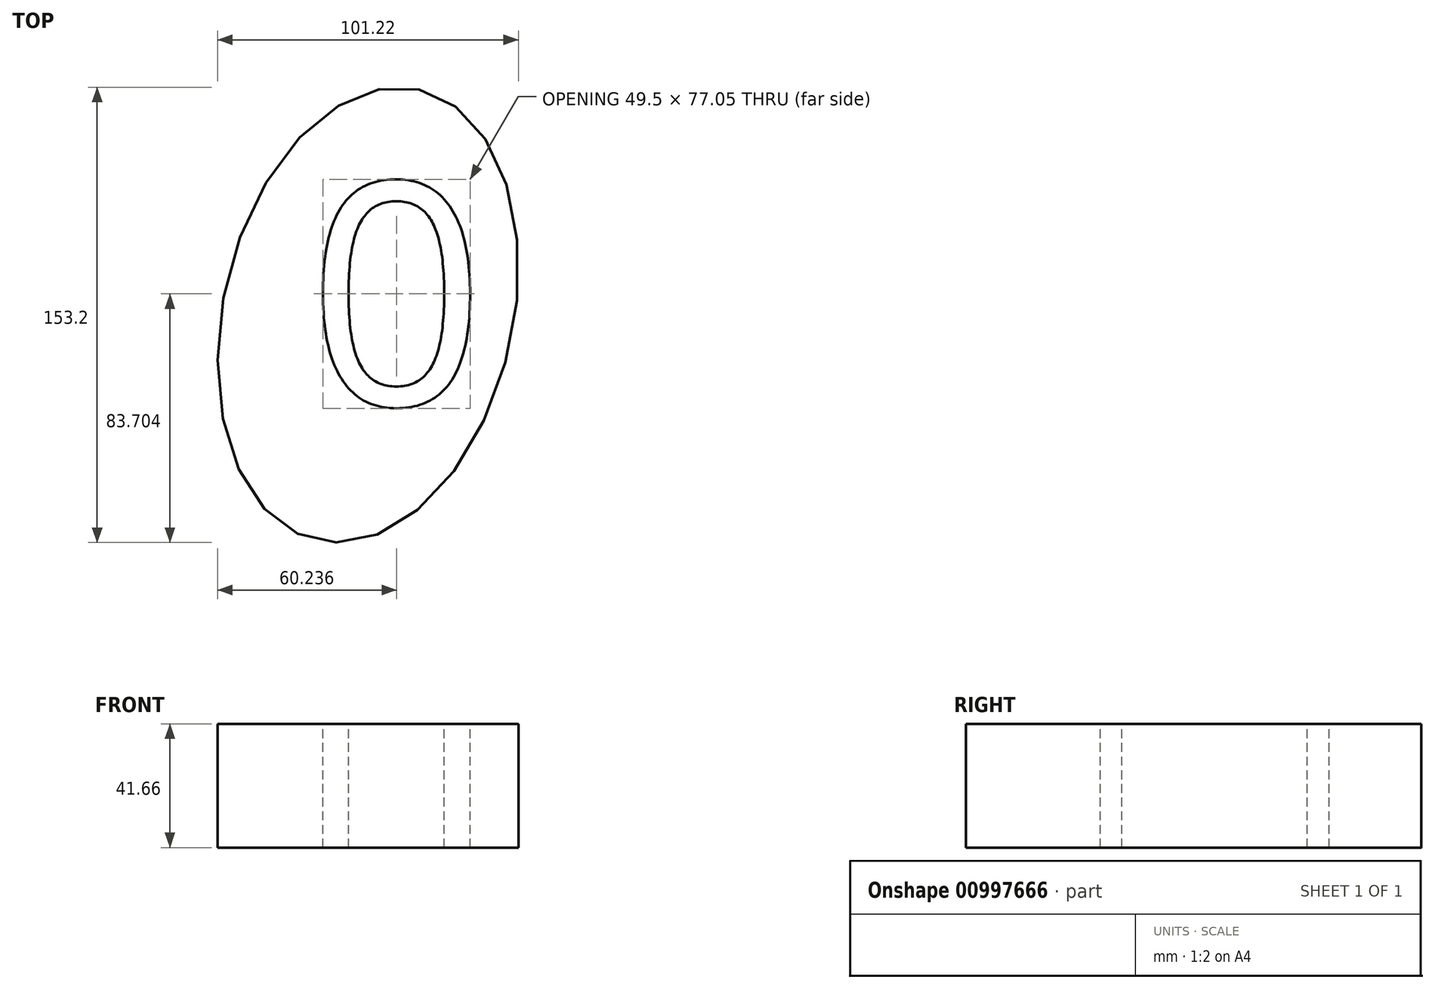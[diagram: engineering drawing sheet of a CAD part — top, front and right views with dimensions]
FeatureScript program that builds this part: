
annotation { "Feature Type Name" : "Feature", "Feature Type Description" : "" }
export const myFeature = defineFeature(function(context is Context, id is Id, definition is map)
    precondition{}
    {
        {
            var Q0;
            Q0=qCreatedBy(makeId("Top.planeOp"),FACE);
            var sketch = newSketch(context, id + "F0", { "sketchPlane" : qUnion([Q0])});
            skEllipse(sketch, "E0", {"center": v(0, 0) * mm, "majorRadius": 77.77 * mm, "minorRadius": 48.8 * mm, "majorAxis": v(0.22, 0.98)});
            skSolve(sketch);
        }
        {
            var Q0;
            Q0=makeQuery(id+"F0.imprint","IMPRINT",FACE,{"disambiguationData":[TD([[makeQuery(id+"F0.imprint","IMPRINT",EDGE,{"derivedFrom":sQuery(id+"F0.wireOp",EDGE,"E0")}),1.0]])]});
            extrude(context, id + "F1", {"entities" : qUnion([Q0]), "depth" : 41.66 * mm, "offsetDistance" : 25.4 * mm});
        }
        {
            var Q0;
            Q0=makeQuery(id+"F1.opExtrude","CAP_FACE",FACE,{"disambiguationData":[OSD([sQuery(id+"F0.wireOp",EDGE,"E0")])],"isStart":false});
            var sketch = newSketch(context, id + "F2", { "sketchPlane" : qUnion([Q0])});
            skText(sketch, "E1", { "text": "0\n\n", "fontName": "OpenSans-Regular.ttf"});
            const initialGuessF2  = {"E1": [-0.02035, -0.03039, 1, 0, 0.07548]};
            skSetInitialGuess(sketch, initialGuessF2);
            skSolve(sketch);
        }
        {
            var Q0;
            Q0 = qSketchRegion(id + "F2", true);
            extrude(context, id + "F3", {"entities" : qUnion([Q0]), "operationType" : NewBodyOperationType.REMOVE, "endBound" : BoundingType.THROUGH_ALL, "oppositeDirection" : true, "depth" : 25.4 * mm, "offsetDistance" : 25.4 * mm});
        }
    });
